# Revit family: Keilhauer-GSD-Bench-2_Seater-Low_Back-
name_source: partatom
category: Furniture
revit_build: Autodesk Revit 2016 (Build: 20150220_1215(x64)
units: mm (PartAtom-declared; Revit-internal decimal feet)

## family parameters
Always vertical = Yes
Cut with Voids When Loaded = No
OmniClass Number = 23.40.20.00
OmniClass Title = General Furniture and Specialties
Room Calculation Point = No
Shared = No
Work Plane-Based = No

## types (9) — shared parameters
Assembly Code = E2020200
Cushion W = 31"
Depth = 26"
Height = 36"
Keynote = 12500
Leg Dist = 5 1/2"
Low Emitting Finish = Yes
Low Emitting Material = Yes
Manufacturer = Keilhauer
Product Documentation Link = https://keilhauer.com
Revit File Built By = https://servex-us.com
Salvage or Reuse = Yes
Type Comments = GSD
URL = https://keilhauer.com
Width = 62"
center = No
zero-valued in all types: Percentage of Recycled Content

## per-type parameters (varying)
| type | Arm L | Arm R | Back L | Back R | Description | Seat L | Seat R |
| 88010 | No | No | Yes | Yes | Low back 2-seater bench | No | No |
| 88011 | No | No | No | Yes | Low back 2-seater bench with LAF cushion | No | No |
| 88012 | No | No | Yes | No | Low back 2-seater bench with RAF cushion | No | No |
| 88013 | No | No | Yes | Yes | Low back 2-seater bench with two ends | Yes | Yes |
| 88014 | No | No | Yes | Yes | Low back 2-seater bench with LAF end | Yes | No |
| 88015 | No | No | Yes | Yes | Low back 2-seater bench with RAF end | No | Yes |
| 88016 | Yes | Yes | Yes | Yes | Low back 2-seater bench with two arms | No | No |
| 88017 | Yes | No | Yes | Yes | Low back 2-seater bench with LAF arm | No | No |
| 88018 | No | Yes | Yes | Yes | Low back 2-seater bench with RAF arm | No | No |

note: column(s) folded — value = type name in every type: Model

## geometry (parser evidence)
native form markers: Sweep x10
no freeform markers — native parametric forms only
